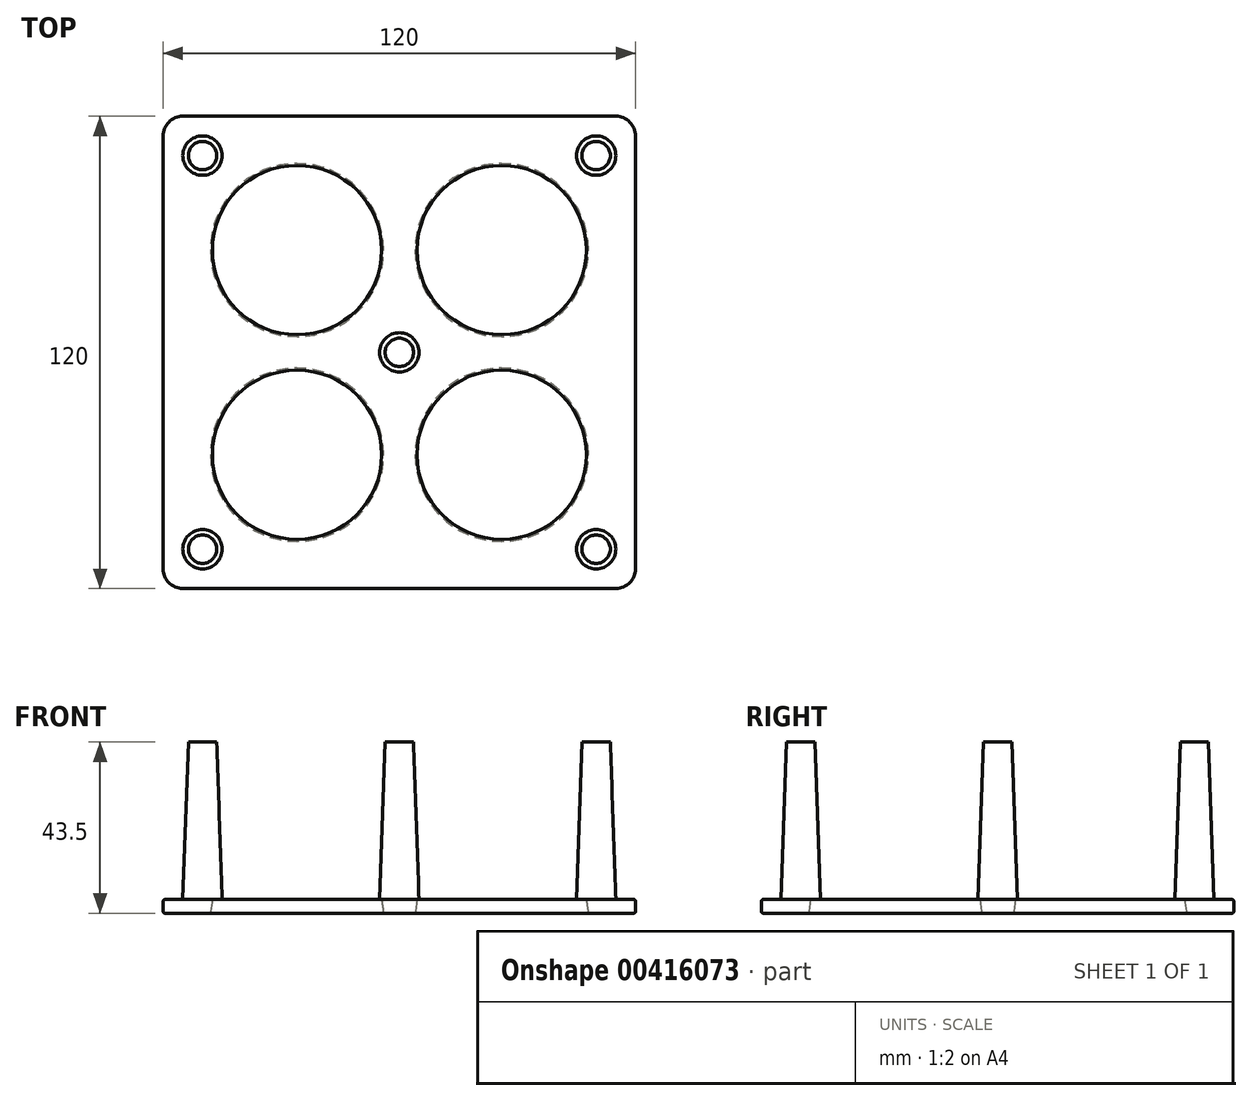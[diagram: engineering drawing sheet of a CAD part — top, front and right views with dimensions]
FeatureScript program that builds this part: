
annotation { "Feature Type Name" : "Feature", "Feature Type Description" : "" }
export const myFeature = defineFeature(function(context is Context, id is Id, definition is map)
    precondition{}
    {
        {
            var Q0;
            Q0=qCreatedBy(makeId("Top.planeOp"),FACE);
            var sketch = newSketch(context, id + "F0", { "sketchPlane" : qUnion([Q0])});
            skLineSegment(sketch, "E0.bottom", {"start": v(-60, 60) * mm, "end": v(60, 60) * mm});
            skLineSegment(sketch, "E0.top", {"start": v(-60, -60) * mm, "end": v(60, -60) * mm});
            skLineSegment(sketch, "E0.left", {"start": v(-60, 60) * mm, "end": v(-60, -60) * mm});
            skLineSegment(sketch, "E0.right", {"start": v(60, 60) * mm, "end": v(60, -60) * mm});
            skPoint(sketch, "E0.middle", {"position": v(0, 0) * mm});
            skCircle(sketch, "E1", {"center": v(-50, 50) * mm, "radius": 5 * mm});
            skCircle(sketch, "E2", {"center": v(-26, 26) * mm, "radius": 21.5 * mm});
            skCircle(sketch, "E3", {"center": v(0, 0) * mm, "radius": 5 * mm});
            skCircle(sketch, "E4.0.1.0", {"center": v(-26, -26) * mm, "radius": 21.5 * mm});
            skCircle(sketch, "E4.1.0.0", {"center": v(26, 26) * mm, "radius": 21.5 * mm});
            skCircle(sketch, "E4.1.1.0", {"center": v(26, -26) * mm, "radius": 21.5 * mm});
            skLineSegment(sketch, "E4.direction1", {"start": v(-26, 26) * mm, "end": v(26, 26) * mm, "construction": true});
            skLineSegment(sketch, "E4.direction2", {"start": v(-26, 26) * mm, "end": v(-26, -26) * mm, "construction": true});
            skCircle(sketch, "E5.0.1.0", {"center": v(-50, -50) * mm, "radius": 5 * mm});
            skCircle(sketch, "E5.1.0.0", {"center": v(50, 50) * mm, "radius": 5 * mm});
            skCircle(sketch, "E5.1.1.0", {"center": v(50, -50) * mm, "radius": 5 * mm});
            skLineSegment(sketch, "E5.direction1", {"start": v(-50, 50) * mm, "end": v(50, 50) * mm, "construction": true});
            skLineSegment(sketch, "E5.direction2", {"start": v(-50, 50) * mm, "end": v(-50, -50) * mm, "construction": true});
            skSolve(sketch);
        }
        {
            var Q0;
            Q0=makeQuery(id+"F0.imprint","IMPRINT",FACE,{"disambiguationData":[TD([[makeQuery(id+"F0.imprint","IMPRINT",EDGE,{"derivedFrom":sQuery(id+"F0.wireOp",EDGE,"E0.bottom")}),-1.0]])]});
            var Q1;
            Q1=makeQuery(id+"F0.imprint","IMPRINT",FACE,{"disambiguationData":[TD([[makeQuery(id+"F0.imprint","IMPRINT",EDGE,{"derivedFrom":sQuery(id+"F0.wireOp",EDGE,"E1")}),1.0]])]});
            var Q2;
            Q2=makeQuery(id+"F0.imprint","IMPRINT",FACE,{"disambiguationData":[TD([[makeQuery(id+"F0.imprint","IMPRINT",EDGE,{"derivedFrom":sQuery(id+"F0.wireOp",EDGE,"E3")}),1.0]])]});
            var Q3;
            Q3=makeQuery(id+"F0.imprint","IMPRINT",FACE,{"disambiguationData":[TD([[makeQuery(id+"F0.imprint","IMPRINT",EDGE,{"derivedFrom":sQuery(id+"F0.wireOp",EDGE,"E5.1.0.0")}),1.0]])]});
            var Q4;
            Q4=makeQuery(id+"F0.imprint","IMPRINT",FACE,{"disambiguationData":[TD([[makeQuery(id+"F0.imprint","IMPRINT",EDGE,{"derivedFrom":sQuery(id+"F0.wireOp",EDGE,"E5.0.1.0")}),1.0]])]});
            var Q5;
            Q5=makeQuery(id+"F0.imprint","IMPRINT",FACE,{"disambiguationData":[TD([[makeQuery(id+"F0.imprint","IMPRINT",EDGE,{"derivedFrom":sQuery(id+"F0.wireOp",EDGE,"E5.1.1.0")}),1.0]])]});
            extrude(context, id + "F1", {"entities" : qUnion([Q0, Q1, Q2, Q3, Q4, Q5]), "oppositeDirection" : true, "depth" : 3.5 * mm});
        }
        {
            var Q0;
            Q0=makeQuery(id+"F0.imprint","IMPRINT",FACE,{"disambiguationData":[TD([[makeQuery(id+"F0.imprint","IMPRINT",EDGE,{"derivedFrom":sQuery(id+"F0.wireOp",EDGE,"E1")}),1.0]])]});
            var Q1;
            Q1=makeQuery(id+"F0.imprint","IMPRINT",FACE,{"disambiguationData":[TD([[makeQuery(id+"F0.imprint","IMPRINT",EDGE,{"derivedFrom":sQuery(id+"F0.wireOp",EDGE,"E3")}),1.0]])]});
            var Q2;
            Q2=makeQuery(id+"F0.imprint","IMPRINT",FACE,{"disambiguationData":[TD([[makeQuery(id+"F0.imprint","IMPRINT",EDGE,{"derivedFrom":sQuery(id+"F0.wireOp",EDGE,"E5.1.0.0")}),1.0]])]});
            var Q3;
            Q3=makeQuery(id+"F0.imprint","IMPRINT",FACE,{"disambiguationData":[TD([[makeQuery(id+"F0.imprint","IMPRINT",EDGE,{"derivedFrom":sQuery(id+"F0.wireOp",EDGE,"E5.1.1.0")}),1.0]])]});
            var Q4;
            Q4=makeQuery(id+"F0.imprint","IMPRINT",FACE,{"disambiguationData":[TD([[makeQuery(id+"F0.imprint","IMPRINT",EDGE,{"derivedFrom":sQuery(id+"F0.wireOp",EDGE,"E5.0.1.0")}),1.0]])]});
            extrude(context, id + "F2", {"entities" : qUnion([Q0, Q1, Q2, Q3, Q4]), "operationType" : NewBodyOperationType.ADD, "depth" : 40 * mm, "hasDraft" : true, "draftAngle" : 2 * degree, "draftPullDirection" : true});
        }
        {
            var Q0;
            Q0=makeQuery(id+"F1.opExtrude","SWEPT_EDGE",EDGE,{"disambiguationData":[OSD([sQuery(id+"F0.wireOp",EDGE,"E0.top"),sQuery(id+"F0.wireOp",EDGE,"E0.left")])]});
            var Q1;
            Q1=makeQuery(id+"F1.opExtrude","SWEPT_EDGE",EDGE,{"disambiguationData":[OSD([sQuery(id+"F0.wireOp",EDGE,"E0.bottom"),sQuery(id+"F0.wireOp",EDGE,"E0.left")])]});
            var Q2;
            Q2=makeQuery(id+"F1.opExtrude","SWEPT_EDGE",EDGE,{"disambiguationData":[OSD([sQuery(id+"F0.wireOp",EDGE,"E0.bottom"),sQuery(id+"F0.wireOp",EDGE,"E0.right")])]});
            var Q3;
            Q3=makeQuery(id+"F1.opExtrude","SWEPT_EDGE",EDGE,{"disambiguationData":[OSD([sQuery(id+"F0.wireOp",EDGE,"E0.top"),sQuery(id+"F0.wireOp",EDGE,"E0.right")])]});
            fillet(context, id + "F3", {"entities" : qUnion([Q0, Q1, Q2, Q3]), "radius" : 5 * mm, "tangentPropagation" : true, "allowEdgeOverflow" : false});
        }
        {
            var Q0;
            Q0=makeQuery(id+"F1.opExtrude","CAP_EDGE",EDGE,{"disambiguationData":[OSD([sQuery(id+"F0.wireOp",EDGE,"E4.1.0.0")])],"isStart":false});
            var Q1;
            Q1=makeQuery(id+"F1.opExtrude","CAP_EDGE",EDGE,{"disambiguationData":[OSD([sQuery(id+"F0.wireOp",EDGE,"E2")])],"isStart":false});
            var Q2;
            Q2=makeQuery(id+"F1.opExtrude","CAP_EDGE",EDGE,{"disambiguationData":[OSD([sQuery(id+"F0.wireOp",EDGE,"E4.0.1.0")])],"isStart":false});
            var Q3;
            Q3=makeQuery(id+"F1.opExtrude","CAP_EDGE",EDGE,{"disambiguationData":[OSD([sQuery(id+"F0.wireOp",EDGE,"E4.1.1.0")])],"isStart":false});
            chamfer(context, id + "F4", {"entities" : qUnion([Q0, Q1, Q2, Q3]), "chamferType" : ChamferType.TWO_OFFSETS, "width1" : 0.5 * mm, "oppositeDirection" : false, "width2" : 3.5 * mm, "tangentPropagation" : true});
        }
        {
            var Q0;
            Q0=makeQuery(id+"F1.opExtrude","CAP_EDGE",EDGE,{"disambiguationData":[OSD([sQuery(id+"F0.wireOp",EDGE,"E0.top")])],"isStart":false});
            var Q1;
            Q1=makeQuery(id+"F1.opExtrude","CAP_EDGE",EDGE,{"disambiguationData":[OSD([sQuery(id+"F0.wireOp",EDGE,"E0.top")])],"isStart":true});
            fillet(context, id + "F5", {"entities" : qUnion([Q0, Q1]), "radius" : 0.5 * mm, "tangentPropagation" : true, "allowEdgeOverflow" : false});
        }
    });
